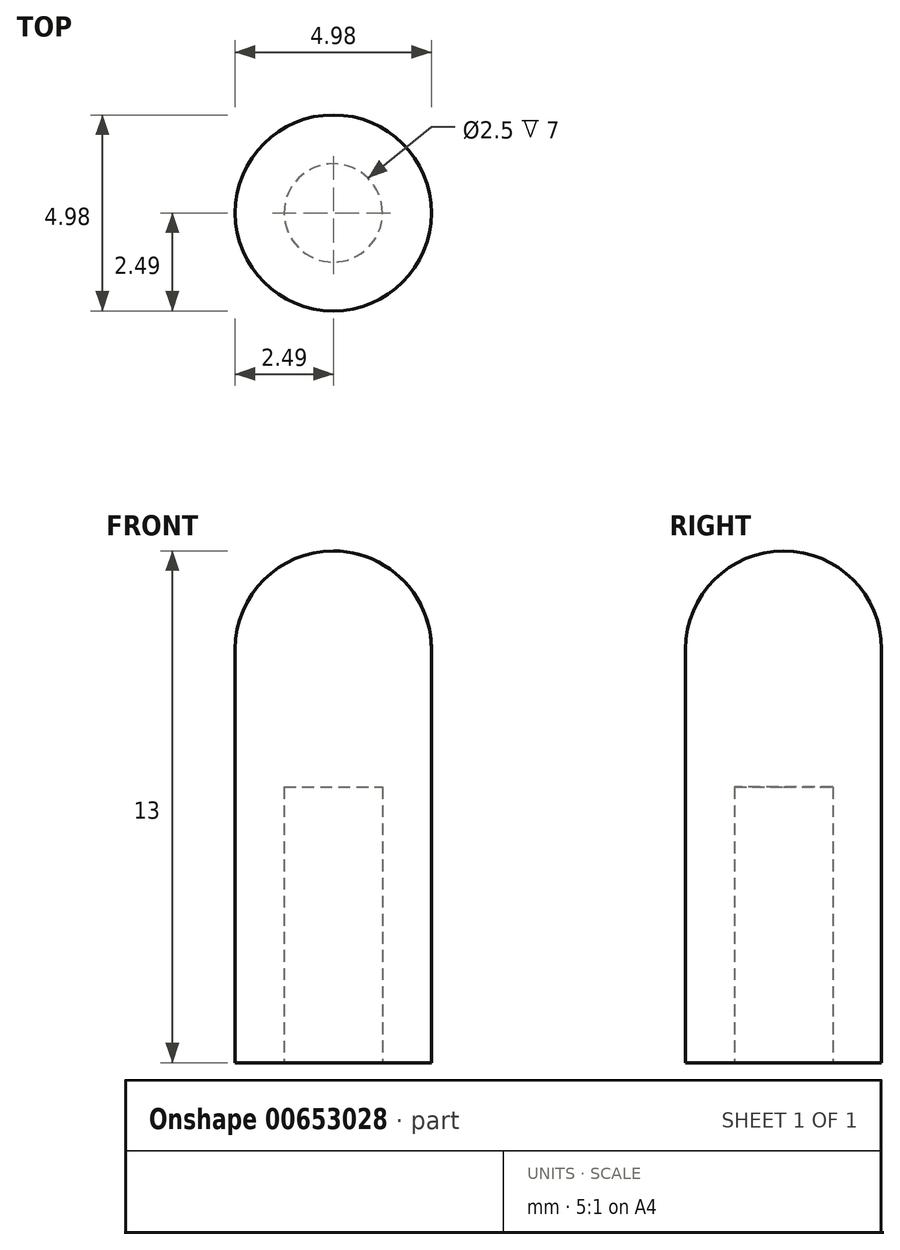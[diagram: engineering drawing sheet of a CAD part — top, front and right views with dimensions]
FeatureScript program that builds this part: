
annotation { "Feature Type Name" : "Feature", "Feature Type Description" : "" }
export const myFeature = defineFeature(function(context is Context, id is Id, definition is map)
    precondition{}
    {
        {
            var Q0;
            Q0=qCreatedBy(makeId("Top.planeOp"),FACE);
            var sketch = newSketch(context, id + "F0", { "sketchPlane" : qUnion([Q0])});
            skCircle(sketch, "E0", {"center": v(0, 0) * mm, "radius": 2.5 * mm});
            skSolve(sketch);
        }
        {
            var Q0;
            Q0=makeQuery(id+"F0.imprint","IMPRINT",FACE,{"disambiguationData":[TD([[makeQuery(id+"F0.imprint","IMPRINT",EDGE,{"derivedFrom":sQuery(id+"F0.wireOp",EDGE,"E0")}),1.0]])]});
            extrude(context, id + "F1", {"entities" : qUnion([Q0]), "depth" : 13 * mm, "offsetDistance" : 25 * mm});
        }
        {
            var Q0;
            Q0=makeQuery(id+"F1.opExtrude","CAP_FACE",FACE,{"disambiguationData":[OSD([sQuery(id+"F0.wireOp",EDGE,"E0")])],"isStart":true});
            var sketch = newSketch(context, id + "F2", { "sketchPlane" : qUnion([Q0])});
            skCircle(sketch, "E1", {"center": v(0, 0) * mm, "radius": 1.25 * mm});
            skSolve(sketch);
        }
        {
            var Q0;
            Q0=makeQuery(id+"F2.imprint","IMPRINT",FACE,{"disambiguationData":[TD([[makeQuery(id+"F2.imprint","IMPRINT",EDGE,{"derivedFrom":sQuery(id+"F2.wireOp",EDGE,"E1")}),1.0]])]});
            extrude(context, id + "F3", {"entities" : qUnion([Q0]), "operationType" : NewBodyOperationType.REMOVE, "oppositeDirection" : true, "depth" : 7 * mm, "offsetDistance" : 25 * mm});
        }
        {
            var Q0;
            Q0=makeQuery(id+"F1.opExtrude","CAP_EDGE",EDGE,{"disambiguationData":[OSD([sQuery(id+"F0.wireOp",EDGE,"E0")])],"isStart":false});
            fillet(context, id + "F4", {"entities" : qUnion([Q0]), "radius" : 2.5 * mm, "tangentPropagation" : true, "allowEdgeOverflow" : false});
        }
    });
